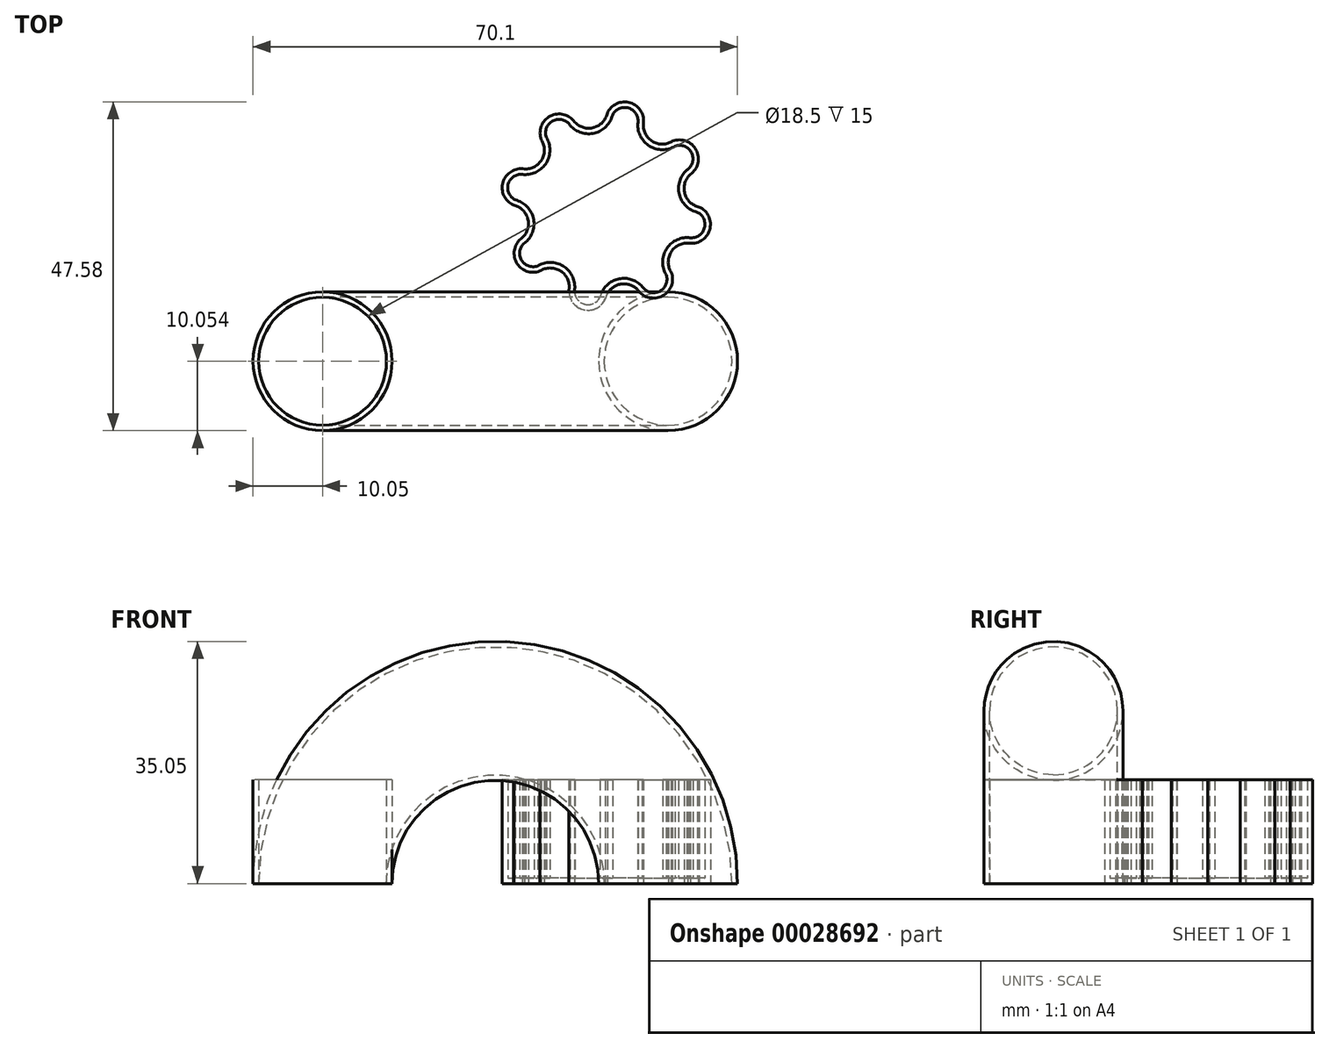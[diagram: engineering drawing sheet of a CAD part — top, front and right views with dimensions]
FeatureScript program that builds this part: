
annotation { "Feature Type Name" : "Feature", "Feature Type Description" : "" }
export const myFeature = defineFeature(function(context is Context, id is Id, definition is map)
    precondition{}
    {
        {
            var Q0;
            Q0=qCreatedBy(makeId("Top.planeOp"),FACE);
            var sketch = newSketch(context, id + "F0", { "sketchPlane" : qUnion([Q0])});
            skCircle(sketch, "E0", {"center": v(0, 0) * mm, "radius": 9.25 * mm, "construction": true});
            skCircle(sketch, "E1.0", {"center": v(0, 0) * mm, "radius": 9.75 * mm, "construction": true});
            skArc(sketch, "E2", {"start": v(-4.7, 7.96) * mm, "mid": v(-1.96, 7.18) * mm, "end": v(0, 9.25) * mm});
            skArc(sketch, "E3", {"start": v(5.22, 7.64) * mm, "mid": v(3.33, 10.77) * mm, "end": v(0, 9.25) * mm});
            skArc(sketch, "E4.1.0", {"start": v(-11.96, 1.18) * mm, "mid": v(-9.46, 2.56) * mm, "end": v(-9.54, 5.41) * mm});
            skArc(sketch, "E4.1.1", {"start": v(-4.7, 7.96) * mm, "mid": v(-8.26, 8.84) * mm, "end": v(-9.54, 5.41) * mm});
            skArc(sketch, "E4.2.0", {"start": v(-12.28, -8.75) * mm, "mid": v(-11.5, -6) * mm, "end": v(-13.57, -4.04) * mm});
            skArc(sketch, "E4.2.1", {"start": v(-11.96, 1.18) * mm, "mid": v(-15.08, -0.72) * mm, "end": v(-13.57, -4.04) * mm});
            skArc(sketch, "E4.3.0", {"start": v(-5.5, -16) * mm, "mid": v(-6.88, -13.5) * mm, "end": v(-9.73, -13.58) * mm});
            skArc(sketch, "E4.3.1", {"start": v(-12.28, -8.75) * mm, "mid": v(-13.16, -12.3) * mm, "end": v(-9.73, -13.58) * mm});
            skArc(sketch, "E4.4.0", {"start": v(4.43, -16.32) * mm, "mid": v(1.69, -15.54) * mm, "end": v(-0.28, -17.61) * mm});
            skArc(sketch, "E4.4.1", {"start": v(-5.5, -16) * mm, "mid": v(-3.6, -19.13) * mm, "end": v(-0.28, -17.61) * mm});
            skArc(sketch, "E4.5.0", {"start": v(11.68, -9.54) * mm, "mid": v(9.19, -10.92) * mm, "end": v(9.26, -13.78) * mm});
            skArc(sketch, "E4.5.1", {"start": v(4.43, -16.32) * mm, "mid": v(7.98, -17.2) * mm, "end": v(9.26, -13.78) * mm});
            skArc(sketch, "E4.6.0", {"start": v(12, 0.39) * mm, "mid": v(11.22, -2.36) * mm, "end": v(13.3, -4.32) * mm});
            skArc(sketch, "E4.6.1", {"start": v(11.68, -9.54) * mm, "mid": v(14.8, -7.65) * mm, "end": v(13.3, -4.32) * mm});
            skArc(sketch, "E4.7.0", {"start": v(5.22, 7.64) * mm, "mid": v(6.6, 5.14) * mm, "end": v(9.46, 5.22) * mm});
            skArc(sketch, "E4.7.1", {"start": v(12, 0.39) * mm, "mid": v(12.88, 3.94) * mm, "end": v(9.46, 5.22) * mm});
            skPoint(sketch, "E4.center", {"position": v(-0.14, -4.18) * mm});
            skSolve(sketch);
        }
        {
            assignVariable(context, id + "F1", {"name" : "height", "anyValue" : 15});
        }
        {
            var Q0;
            Q0=makeQuery(id+"F0.imprint","IMPRINT",FACE,{"disambiguationData":[TD([[makeQuery(id+"F0.imprint","IMPRINT",EDGE,{"derivedFrom":sQuery(id+"F0.wireOp",EDGE,"E2")}),-1.0]])]});
            extrude(context, id + "F2", {"entities" : qUnion([Q0]), "depth" : (getVariable(context, 'height')) * mm});
        }
        {
            var Q0;
            Q0=makeQuery(id+"F2.opExtrude","CAP_FACE",FACE,{"disambiguationData":[OSD([sQuery(id+"F0.wireOp",EDGE,"E2"),sQuery(id+"F0.wireOp",EDGE,"E3"),sQuery(id+"F0.wireOp",EDGE,"E4.1.0"),sQuery(id+"F0.wireOp",EDGE,"E4.1.1"),sQuery(id+"F0.wireOp",EDGE,"E4.2.0"),sQuery(id+"F0.wireOp",EDGE,"E4.2.1"),sQuery(id+"F0.wireOp",EDGE,"E4.3.0"),sQuery(id+"F0.wireOp",EDGE,"E4.3.1"),sQuery(id+"F0.wireOp",EDGE,"E4.4.0"),sQuery(id+"F0.wireOp",EDGE,"E4.4.1"),sQuery(id+"F0.wireOp",EDGE,"E4.5.0"),sQuery(id+"F0.wireOp",EDGE,"E4.5.1"),sQuery(id+"F0.wireOp",EDGE,"E4.6.0"),sQuery(id+"F0.wireOp",EDGE,"E4.6.1"),sQuery(id+"F0.wireOp",EDGE,"E4.7.0"),sQuery(id+"F0.wireOp",EDGE,"E4.7.1")])],"isStart":false});
            shell(context, id + "F3", {"entities" : qUnion([Q0]), "thickness" : .8 * mm});
        }
        {
            var Q0;
            Q0=qCreatedBy(makeId("Top.planeOp"),FACE);
            var sketch = newSketch(context, id + "F4", { "sketchPlane" : qUnion([Q0])});
            skCircle(sketch, "E5", {"center": v(-41.2, -26.64) * mm, "radius": 9.25 * mm});
            skCircle(sketch, "E6.0", {"center": v(-41.2, -26.64) * mm, "radius": 10.05 * mm});
            skSolve(sketch);
        }
        {
            var Q0;
            Q0 = qSketchRegion(id + "F4", true);
            extrude(context, id + "F5", {"entities" : qUnion([Q0]), "depth" : (getVariable(context, 'height')) * mm});
        }
        {
            var Q0;
            Q0=qCreatedBy(makeId("Front.planeOp"),FACE);
            var sketch = newSketch(context, id + "F6", { "sketchPlane" : qUnion([Q0])});
            skArc(sketch, "E7", {"start": v(8.8, 0) * mm, "mid": v(-16.2, 25) * mm, "end": v(-41.2, 0) * mm});
            skSolve(sketch);
        }
        {
            var Q0;
            Q0=makeQuery(id+"F4.imprint","IMPRINT",FACE,{"disambiguationData":[TD([[makeQuery(id+"F4.imprint","IMPRINT",EDGE,{"derivedFrom":sQuery(id+"F4.wireOp",EDGE,"E5")}),-1.0]])]});
            var Q1;
            Q1=sQuery(id+"F6.wireOp",EDGE,"E7");
            sweep(context, id + "F7", {"profiles" : qUnion([Q0]), "path" : qUnion([Q1])});
        }
    });
